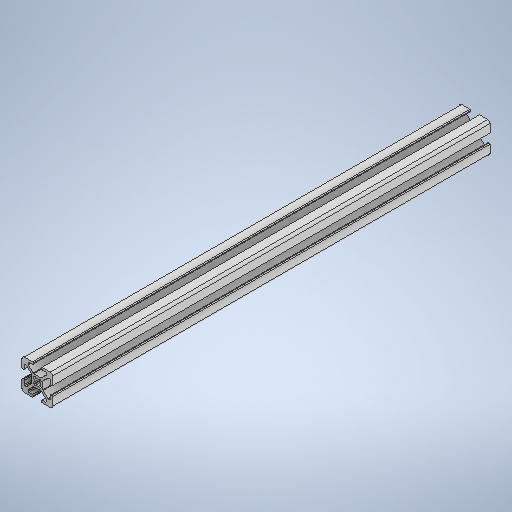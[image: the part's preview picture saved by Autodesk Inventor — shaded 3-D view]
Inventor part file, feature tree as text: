
AUTODESK INVENTOR PART (.ipt)
format: ipt  version: 2025 (Build 290162000, 162)  size: 473,600 bytes
history: native  units: mm
features: sketch x2, extrude x1, hole x1, mirror x1
ambient origin geometry x8: Origin, YZ Plane, XZ Plane, XY Plane, X Axis, Y Axis, Z Axis, Center Point
bodies: Solid1 (feature_tree)
feature tree (5):
  extrude  "Extrusion1"  Depth=2.384mm
  hole  "Hole1"  [1 undecoded]
  mirror  "Mirror1"
  sketch  "Sketch1"  dims[d0=285.29mm d1=0.0mm]
  sketch  "Sketch2"  dims[d2=5.0mm d3=6.0mm d4=4.0mm d5=2.0mm d6=90.0deg d7=8.0mm d8=20.594885mm d9=2.384mm d10=8.0mm d11=0.0625mm d12=0.75mm d13=0.375mm]
note: 1 required parameter value undecoded (feature->parameter linkage not recoverable at this tier; creation-order binding heuristic only, values carry confidence <= 0.55)
